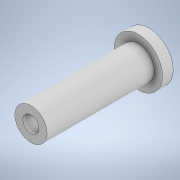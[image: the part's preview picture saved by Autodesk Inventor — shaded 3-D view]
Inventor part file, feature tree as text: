
AUTODESK INVENTOR PART (.ipt)
format: ipt  version: 2020.1 (Build 241239000, 239)  size: 113,664 bytes
history: native  units: mm
features: extrude x3, sketch x3
ambient origin geometry x8: Origin, YZ Plane, XZ Plane, XY Plane, X Axis, Y Axis, Z Axis, Center Point
bodies: Solid1 (feature_tree)
feature tree (6):
  extrude  "Extrusion1"  Depth=4.0mm TaperAngle=0.0deg
  extrude  "Extrusion2"  Depth=6.0mm
  extrude  "Extrusion3"  Depth=25.5mm TaperAngle=0.0deg
  sketch  "Sketch1"  dims[d0=18.0mm d1=4.0mm d2=0.0mm]
  sketch  "Sketch2"  dims[d3=12.0mm d4=6.0mm]
  sketch  "Sketch4"  dims[d5=40.0mm d6=0.0mm d8=25.5mm d9=0.0mm]
